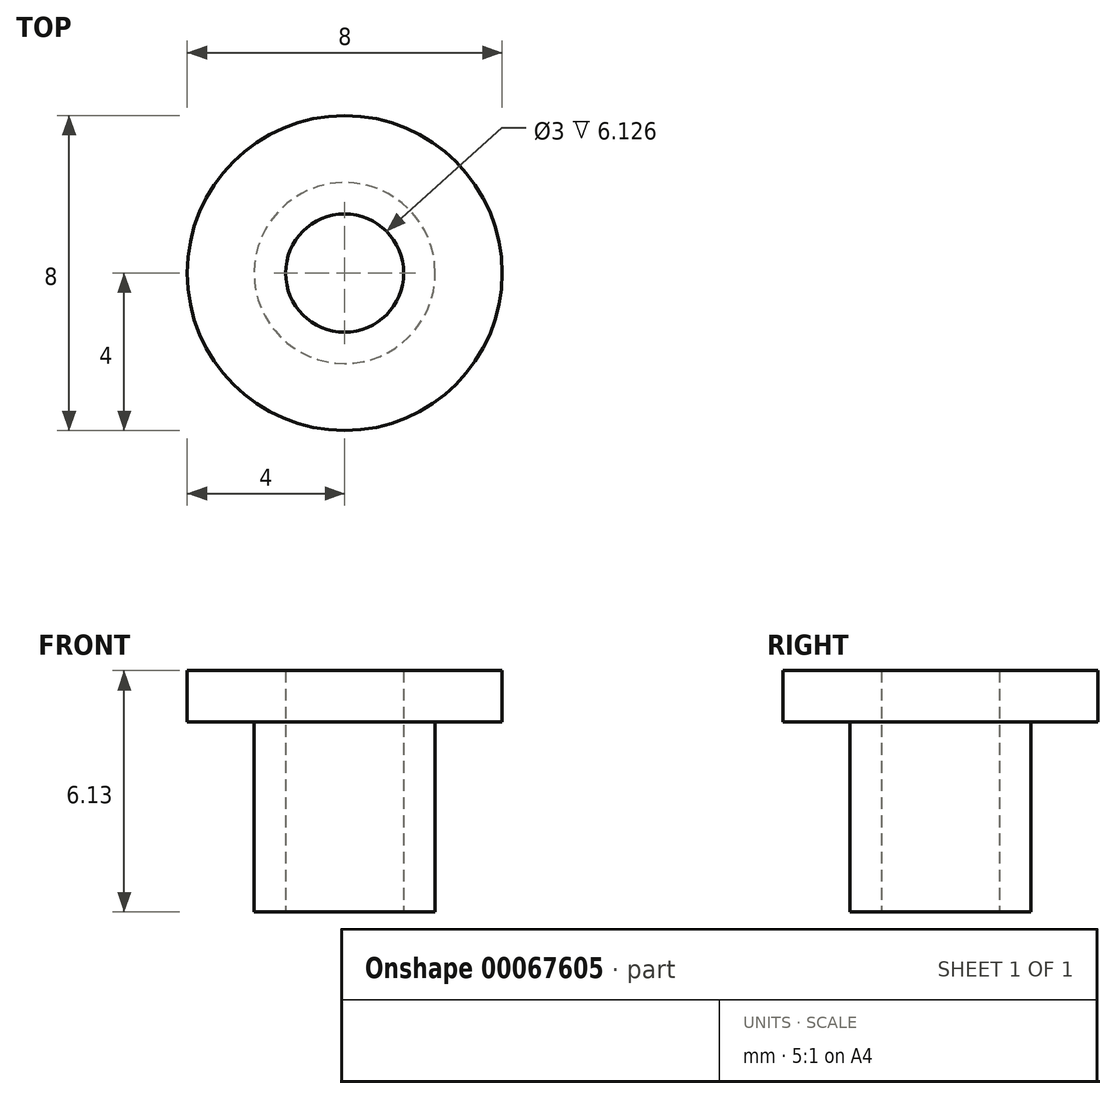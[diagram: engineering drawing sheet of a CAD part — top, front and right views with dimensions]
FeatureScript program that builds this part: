
annotation { "Feature Type Name" : "Feature", "Feature Type Description" : "" }
export const myFeature = defineFeature(function(context is Context, id is Id, definition is map)
    precondition{}
    {
        {
            var Q0;
            Q0=qCreatedBy(makeId("Top.planeOp"),FACE);
            var sketch = newSketch(context, id + "F0", { "sketchPlane" : qUnion([Q0])});
            skCircle(sketch, "E0", {"center": v(0, 0) * mm, "radius": 4 * mm});
            skCircle(sketch, "E1", {"center": v(0, 0) * mm, "radius": 1.5 * mm});
            skCircle(sketch, "E2", {"center": v(0, 0) * mm, "radius": 2.3 * mm});
            skSolve(sketch);
        }
        {
            var Q0;
            Q0 = qSketchRegion(id + "F0", true);
            var Q1;
            Q1=makeQuery(id+"F0.imprint","IMPRINT",FACE,{"disambiguationData":[TD([[makeQuery(id+"F0.imprint","IMPRINT",EDGE,{"derivedFrom":sQuery(id+"F0.wireOp",EDGE,"E1")}),-1.0]])]});
            extrude(context, id + "F1", {"entities" : qUnion([Q0, Q1]), "depth" : 1.3 * mm});
        }
        {
            var Q0;
            Q0=makeQuery(id+"F0.imprint","IMPRINT",FACE,{"disambiguationData":[TD([[makeQuery(id+"F0.imprint","IMPRINT",EDGE,{"derivedFrom":sQuery(id+"F0.wireOp",EDGE,"E1")}),-1.0]])]});
            extrude(context, id + "F2", {"entities" : qUnion([Q0]), "operationType" : NewBodyOperationType.ADD, "oppositeDirection" : true, "depth" : 4.83 * mm});
        }
    });
